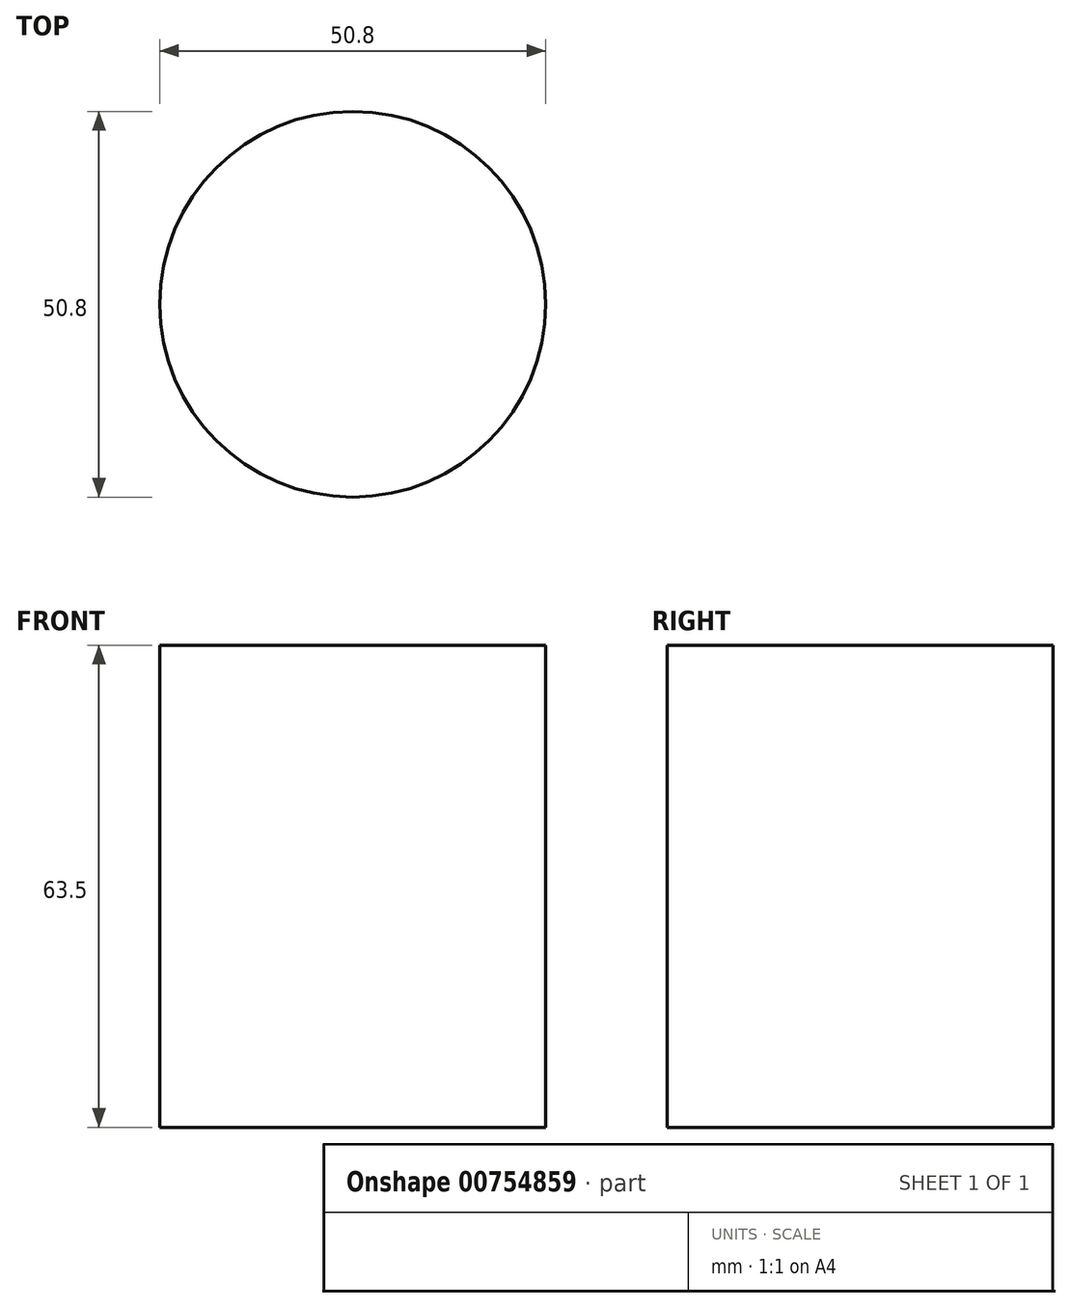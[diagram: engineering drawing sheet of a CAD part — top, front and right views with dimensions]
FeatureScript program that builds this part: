
annotation { "Feature Type Name" : "Feature", "Feature Type Description" : "" }
export const myFeature = defineFeature(function(context is Context, id is Id, definition is map)
    precondition{}
    {
        {
            var Q0;
            Q0=qCreatedBy(makeId("Top.planeOp"),FACE);
            var sketch = newSketch(context, id + "F0", { "sketchPlane" : qUnion([Q0])});
            skCircle(sketch, "E0", {"center": v(-72.51, 0) * mm, "radius": 25.4 * mm});
            skSolve(sketch);
        }
        {
            var Q0;
            Q0=makeQuery(id+"F0.imprint","IMPRINT",FACE,{"disambiguationData":[TD([[makeQuery(id+"F0.imprint","IMPRINT",EDGE,{"derivedFrom":sQuery(id+"F0.wireOp",EDGE,"E0")}),1.0]])]});
            extrude(context, id + "F1", {"entities" : qUnion([Q0]), "depth" : 63.5 * mm, "offsetDistance" : 25.4 * mm});
        }
    });
